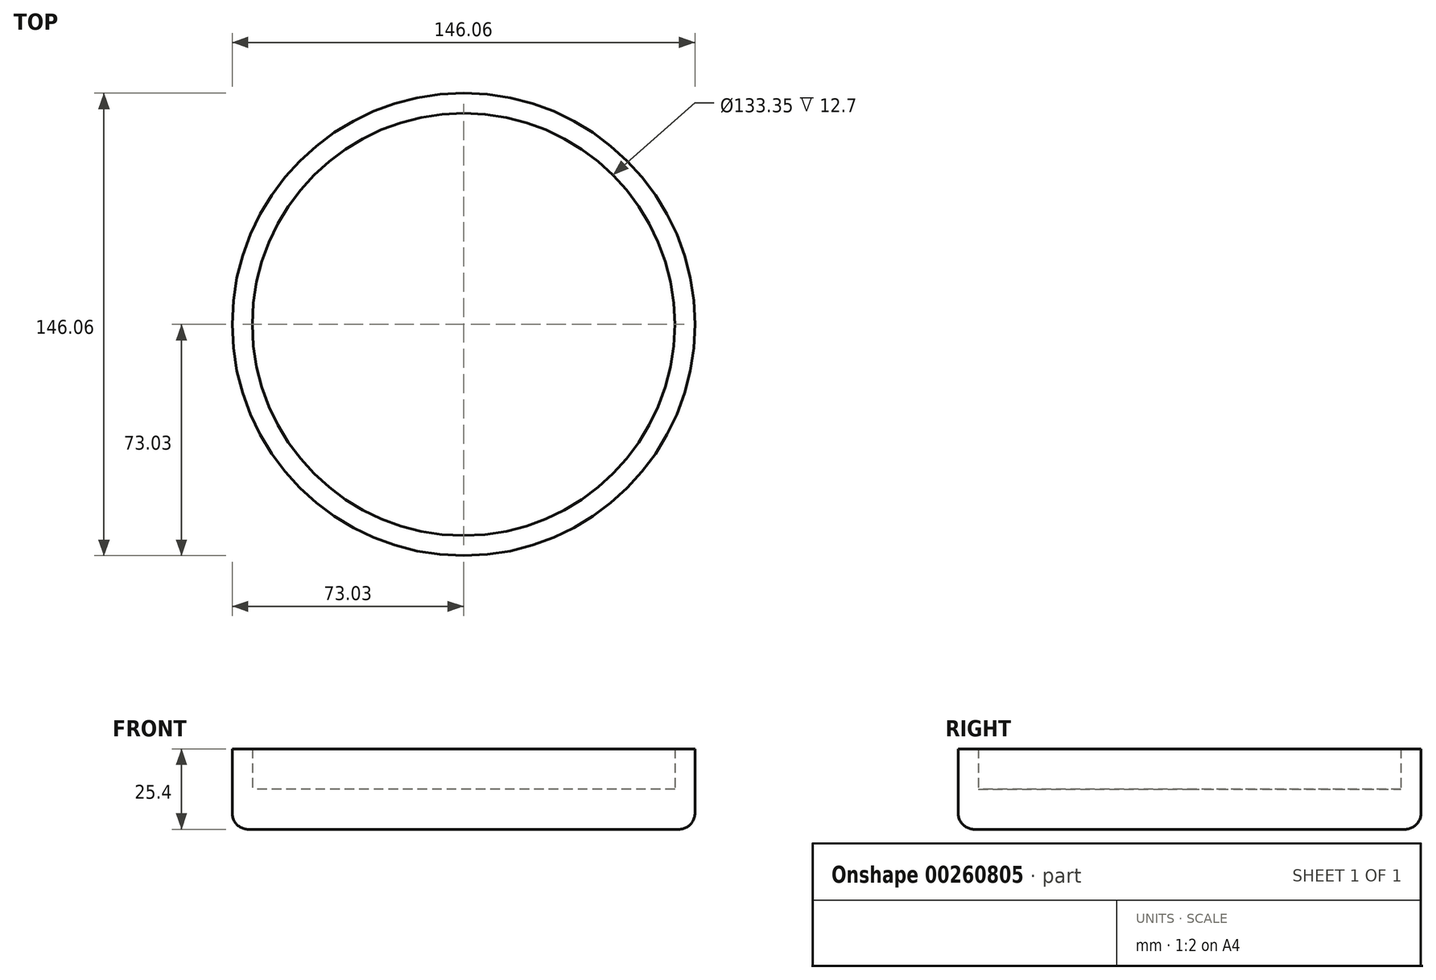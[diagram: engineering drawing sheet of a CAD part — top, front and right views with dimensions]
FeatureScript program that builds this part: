
annotation { "Feature Type Name" : "Feature", "Feature Type Description" : "" }
export const myFeature = defineFeature(function(context is Context, id is Id, definition is map)
    precondition{}
    {
        {
            var Q0;
            Q0=qCreatedBy(makeId("Top.planeOp"),FACE);
            var sketch = newSketch(context, id + "F0", { "sketchPlane" : qUnion([Q0])});
            skCircle(sketch, "E0", {"center": v(0, 0) * mm, "radius": 73.03 * mm});
            skCircle(sketch, "E1", {"center": v(0, 0) * mm, "radius": 66.68 * mm});
            skSolve(sketch);
        }
        {
            var Q0;
            Q0 = qSketchRegion(id + "F0", true);
            extrude(context, id + "F1", {"entities" : qUnion([Q0]), "depth" : 25.4 * mm});
        }
        {
            var Q0;
            Q0=qCreatedBy(makeId("Top.planeOp"),FACE);
            var sketch = newSketch(context, id + "F2", { "sketchPlane" : qUnion([Q0])});
            skCircle(sketch, "E2", {"center": v(0, 0) * mm, "radius": 66.68 * mm});
            skSolve(sketch);
        }
        {
            var Q0;
            Q0=makeQuery(id+"F2.imprint","IMPRINT",FACE,{"disambiguationData":[TD([[makeQuery(id+"F2.imprint","IMPRINT",EDGE,{"derivedFrom":sQuery(id+"F2.wireOp",EDGE,"E2")}),1.0]])]});
            extrude(context, id + "F3", {"entities" : qUnion([Q0]), "operationType" : NewBodyOperationType.ADD, "depth" : 12.7 * mm});
        }
        {
            var Q0;
            Q0=makeQuery(id+"F1.opExtrude","CAP_EDGE",EDGE,{"disambiguationData":[OSD([sQuery(id+"F0.wireOp",EDGE,"E0")])],"isStart":true});
            fillet(context, id + "F4", {"entities" : qUnion([Q0]), "radius" : 5.08 * mm, "tangentPropagation" : true, "allowEdgeOverflow" : false});
        }
    });
